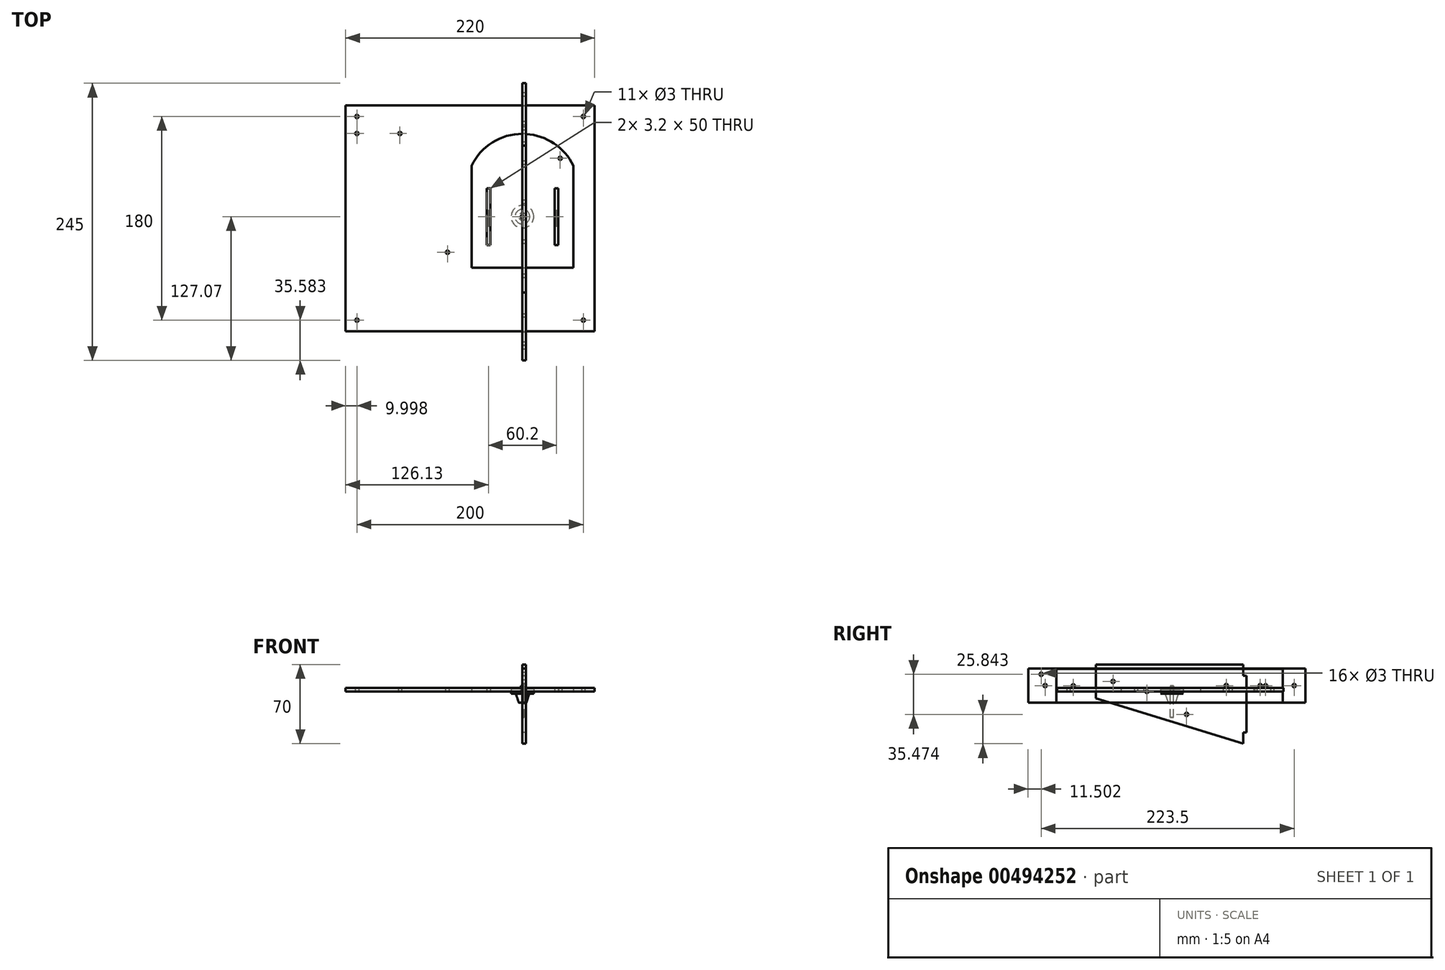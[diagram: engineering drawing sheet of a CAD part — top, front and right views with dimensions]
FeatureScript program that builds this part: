
annotation { "Feature Type Name" : "Feature", "Feature Type Description" : "" }
export const myFeature = defineFeature(function(context is Context, id is Id, definition is map)
    precondition{}
    {
        {
            var Q0;
            Q0=qCreatedBy(makeId("Right.planeOp"),FACE);
            var sketch = newSketch(context, id + "F0", { "sketchPlane" : qUnion([Q0])});
            skLineSegment(sketch, "E0", {"start": v(-67.11, 23.84) * mm, "end": v(62.89, 23.84) * mm});
            skLineSegment(sketch, "E1", {"start": v(-67.11, 23.84) * mm, "end": v(-67.11, -6.16) * mm});
            skLineSegment(sketch, "E2", {"start": v(62.89, 23.84) * mm, "end": v(62.89, -46.16) * mm});
            skLineSegment(sketch, "E3", {"start": v(-67.11, -6.16) * mm, "end": v(62.89, -46.16) * mm});
            skLineSegment(sketch, "E4.bottom", {"start": v(62.89, 13.84) * mm, "end": v(65.89, 13.84) * mm});
            skLineSegment(sketch, "E4.top", {"start": v(62.89, -36.16) * mm, "end": v(65.89, -36.16) * mm});
            skLineSegment(sketch, "E4.left", {"start": v(62.89, 13.84) * mm, "end": v(62.89, -36.16) * mm});
            skLineSegment(sketch, "E4.right", {"start": v(65.89, 13.84) * mm, "end": v(65.89, -36.16) * mm});
            skCircle(sketch, "E5", {"center": v(12.89, -20.32) * mm, "radius": 1.5 * mm});
            skSolve(sketch);
        }
        {
            var Q0;
            Q0=qCreatedBy(makeId("Right.planeOp"),FACE);
            var sketch = newSketch(context, id + "F1", { "sketchPlane" : qUnion([Q0])});
            skLineSegment(sketch, "E6.bottom", {"start": v(-127.07, 20.16) * mm, "end": v(117.93, 20.16) * mm});
            skLineSegment(sketch, "E6.top", {"start": v(-127.07, -9.84) * mm, "end": v(117.93, -9.84) * mm});
            skLineSegment(sketch, "E6.left", {"start": v(-127.07, 20.16) * mm, "end": v(-127.07, -9.84) * mm});
            skLineSegment(sketch, "E6.right", {"start": v(117.93, 20.16) * mm, "end": v(117.93, -9.84) * mm});
            skCircle(sketch, "E7", {"center": v(107.93, 5.16) * mm, "radius": 1.5 * mm});
            skCircle(sketch, "E8", {"center": v(77.93, 5.16) * mm, "radius": 1.5 * mm});
            skCircle(sketch, "E9", {"center": v(-115.57, 15.16) * mm, "radius": 1.5 * mm});
            skSolve(sketch);
        }
        {
            var Q0;
            Q0=qCreatedBy(makeId("Right.planeOp"),FACE);
            var sketch = newSketch(context, id + "F2", { "sketchPlane" : qUnion([Q0])});
            skLineSegment(sketch, "E10.bottom", {"start": v(-102.26, 20) * mm, "end": v(97.74, 20) * mm});
            skLineSegment(sketch, "E10.top", {"start": v(-102.26, -10) * mm, "end": v(97.74, -10) * mm});
            skLineSegment(sketch, "E10.left", {"start": v(-102.26, 20) * mm, "end": v(-102.26, -10) * mm});
            skLineSegment(sketch, "E10.right", {"start": v(97.74, 20) * mm, "end": v(97.74, -10) * mm});
            skCircle(sketch, "E11", {"center": v(-22.26, 0) * mm, "radius": 1.5 * mm});
            skSolve(sketch);
        }
        {
            var Q0;
            Q0 = qSketchRegion(id + "F0", true);
            extrude(context, id + "F3", {"entities" : qUnion([Q0]), "depth" : 3.2 * mm});
        }
        {
            var Q0;
            Q0=makeQuery(id+"F1.imprint","IMPRINT",FACE,{"disambiguationData":[TD([[makeQuery(id+"F1.imprint","IMPRINT",EDGE,{"derivedFrom":sQuery(id+"F1.wireOp",EDGE,"E6.bottom")}),-1.0]])]});
            extrude(context, id + "F4", {"entities" : qUnion([Q0]), "depth" : 3.2 * mm});
        }
        {
            var Q0;
            Q0=makeQuery(id+"F2.imprint","IMPRINT",FACE,{"disambiguationData":[TD([[makeQuery(id+"F2.imprint","IMPRINT",EDGE,{"derivedFrom":sQuery(id+"F2.wireOp",EDGE,"E10.bottom")}),-1.0]])]});
            extrude(context, id + "F5", {"entities" : qUnion([Q0]), "depth" : 3.2 * mm});
        }
        {
            var Q0;
            Q0=makeQuery(id+"F3.opExtrude","CAP_FACE",FACE,{"disambiguationData":[OSD([sQuery(id+"F0.wireOp",EDGE,"E0"),sQuery(id+"F0.wireOp",EDGE,"E1"),sQuery(id+"F0.wireOp",EDGE,"E2"),sQuery(id+"F0.wireOp",EDGE,"E3")])],"isStart":false});
            var sketch = newSketch(context, id + "F6", { "sketchPlane" : qUnion([Q0])});
            skCircle(sketch, "E12", {"center": v(-52.11, 8.84) * mm, "radius": 1.5 * mm});
            skSolve(sketch);
        }
        {
            var Q0;
            Q0=makeQuery(id+"F6.imprint","IMPRINT",FACE,{"disambiguationData":[TD([[makeQuery(id+"F6.imprint","IMPRINT",EDGE,{"derivedFrom":sQuery(id+"F6.wireOp",EDGE,"E12")}),1.0]])]});
            extrude(context, id + "F7", {"entities" : qUnion([Q0]), "operationType" : NewBodyOperationType.REMOVE, "endBound" : BoundingType.THROUGH_ALL, "oppositeDirection" : true, "depth" : 25 * mm});
        }
        {
            var Q0;
            Q0=makeQuery(id+"F4.opExtrude","CAP_FACE",FACE,{"disambiguationData":[OSD([sQuery(id+"F1.wireOp",EDGE,"E6.bottom"),sQuery(id+"F1.wireOp",EDGE,"E6.top"),sQuery(id+"F1.wireOp",EDGE,"E6.left"),sQuery(id+"F1.wireOp",EDGE,"E6.right")])],"isStart":false});
            var sketch = newSketch(context, id + "F8", { "sketchPlane" : qUnion([Q0])});
            skCircle(sketch, "E13", {"center": v(-112.07, 5.16) * mm, "radius": 1.5 * mm});
            skCircle(sketch, "E14", {"center": v(47.93, 5.16) * mm, "radius": 1.5 * mm});
            skSolve(sketch);
        }
        {
            var Q0;
            Q0=makeQuery(id+"F8.imprint","IMPRINT",FACE,{"disambiguationData":[TD([[makeQuery(id+"F8.imprint","IMPRINT",EDGE,{"derivedFrom":sQuery(id+"F8.wireOp",EDGE,"E13")}),1.0]])]});
            var Q1;
            Q1=makeQuery(id+"F8.imprint","IMPRINT",FACE,{"disambiguationData":[TD([[makeQuery(id+"F8.imprint","IMPRINT",EDGE,{"derivedFrom":sQuery(id+"F8.wireOp",EDGE,"E14")}),1.0]])]});
            extrude(context, id + "F9", {"entities" : qUnion([Q0, Q1]), "operationType" : NewBodyOperationType.REMOVE, "endBound" : BoundingType.THROUGH_ALL, "oppositeDirection" : true, "depth" : 25 * mm});
        }
        {
            var Q0;
            Q0=makeQuery(id+"F5.opExtrude","CAP_FACE",FACE,{"disambiguationData":[OSD([sQuery(id+"F2.wireOp",EDGE,"E10.bottom"),sQuery(id+"F2.wireOp",EDGE,"E10.top"),sQuery(id+"F2.wireOp",EDGE,"E10.left"),sQuery(id+"F2.wireOp",EDGE,"E10.right")])],"isStart":false});
            var sketch = newSketch(context, id + "F10", { "sketchPlane" : qUnion([Q0])});
            skCircle(sketch, "E15", {"center": v(-87.26, 5) * mm, "radius": 1.5 * mm});
            skCircle(sketch, "E16", {"center": v(82.74, 5) * mm, "radius": 1.5 * mm});
            skSolve(sketch);
        }
        {
            var Q0;
            Q0=makeQuery(id+"F10.imprint","IMPRINT",FACE,{"disambiguationData":[TD([[makeQuery(id+"F10.imprint","IMPRINT",EDGE,{"derivedFrom":sQuery(id+"F10.wireOp",EDGE,"E15")}),1.0]])]});
            var Q1;
            Q1=makeQuery(id+"F10.imprint","IMPRINT",FACE,{"disambiguationData":[TD([[makeQuery(id+"F10.imprint","IMPRINT",EDGE,{"derivedFrom":sQuery(id+"F10.wireOp",EDGE,"E16")}),1.0]])]});
            extrude(context, id + "F11", {"entities" : qUnion([Q0, Q1]), "operationType" : NewBodyOperationType.REMOVE, "endBound" : BoundingType.THROUGH_ALL, "oppositeDirection" : true, "depth" : 25 * mm});
        }
        {
            var Q0;
            Q0=qCreatedBy(makeId("Top.planeOp"),FACE);
            var sketch = newSketch(context, id + "F12", { "sketchPlane" : qUnion([Q0])});
            skLineSegment(sketch, "E17.bottom", {"start": v(-45, 45) * mm, "end": v(45, 45) * mm});
            skLineSegment(sketch, "E17.top", {"start": v(-45, -45) * mm, "end": v(45, -45) * mm});
            skLineSegment(sketch, "E17.left", {"start": v(-45, 45) * mm, "end": v(-45, -45) * mm});
            skLineSegment(sketch, "E17.right", {"start": v(45, 45) * mm, "end": v(45, -45) * mm});
            skLineSegment(sketch, "E18.bottom", {"start": v(-31.7, 25) * mm, "end": v(-28.5, 25) * mm});
            skLineSegment(sketch, "E18.top", {"start": v(-31.7, -25) * mm, "end": v(-28.5, -25) * mm});
            skLineSegment(sketch, "E18.left", {"start": v(-31.7, 25) * mm, "end": v(-31.7, -25) * mm});
            skLineSegment(sketch, "E18.right", {"start": v(-28.5, 25) * mm, "end": v(-28.5, -25) * mm});
            skLineSegment(sketch, "E19.bottom", {"start": v(28.5, 25) * mm, "end": v(31.7, 25) * mm});
            skLineSegment(sketch, "E19.top", {"start": v(28.5, -25) * mm, "end": v(31.7, -25) * mm});
            skLineSegment(sketch, "E19.left", {"start": v(28.5, 25) * mm, "end": v(28.5, -25) * mm});
            skLineSegment(sketch, "E19.right", {"start": v(31.7, 25) * mm, "end": v(31.7, -25) * mm});
            skArc(sketch, "E20", {"start": v(45, 45) * mm, "mid": v(0, 73.2) * mm, "end": v(-45, 45) * mm});
            skCircle(sketch, "E21", {"center": v(33.35, 51.62) * mm, "radius": 1.5 * mm});
            skSolve(sketch);
        }
        {
            var Q0;
            Q0=makeQuery(id+"F12.imprint","IMPRINT",FACE,{"disambiguationData":[TD([[makeQuery(id+"F12.imprint","IMPRINT",EDGE,{"derivedFrom":sQuery(id+"F12.wireOp",EDGE,"E17.bottom")}),-1.0]])]});
            var Q1;
            Q1=makeQuery(id+"F12.imprint","IMPRINT",FACE,{"disambiguationData":[TD([[makeQuery(id+"F12.imprint","IMPRINT",EDGE,{"derivedFrom":sQuery(id+"F12.wireOp",EDGE,"E17.bottom")}),1.0]])]});
            extrude(context, id + "F13", {"entities" : qUnion([Q0, Q1]), "depth" : 3.2 * mm, "offsetDistance" : 25 * mm});
        }
        {
            var Q0;
            Q0=qCreatedBy(makeId("Top.planeOp"),FACE);
            var sketch = newSketch(context, id + "F14", { "sketchPlane" : qUnion([Q0])});
            skLineSegment(sketch, "E22.bottom", {"start": v(-156.23, 98.51) * mm, "end": v(63.77, 98.51) * mm});
            skLineSegment(sketch, "E22.top", {"start": v(-156.23, -101.49) * mm, "end": v(63.77, -101.49) * mm});
            skLineSegment(sketch, "E22.left", {"start": v(-156.23, 98.51) * mm, "end": v(-156.23, -101.49) * mm});
            skLineSegment(sketch, "E22.right", {"start": v(63.77, 98.51) * mm, "end": v(63.77, -101.49) * mm});
            skCircle(sketch, "E23", {"center": v(-146.23, 88.51) * mm, "radius": 1.5 * mm});
            skCircle(sketch, "E24", {"center": v(-146.23, -91.49) * mm, "radius": 1.5 * mm});
            skCircle(sketch, "E25", {"center": v(53.77, 88.51) * mm, "radius": 1.5 * mm});
            skCircle(sketch, "E26", {"center": v(53.77, -91.49) * mm, "radius": 1.5 * mm});
            skCircle(sketch, "E27", {"center": v(-146.23, 73.51) * mm, "radius": 1.5 * mm});
            skCircle(sketch, "E28", {"center": v(-108.23, 73.51) * mm, "radius": 1.5 * mm});
            skSolve(sketch);
        }
        {
            var Q0;
            Q0 = qSketchRegion(id + "F14", true);
            extrude(context, id + "F15", {"entities" : qUnion([Q0]), "depth" : 3 * mm, "offsetDistance" : 25 * mm});
        }
        {
            var Q0;
            Q0=makeQuery(id+"F15.opExtrude","CAP_FACE",FACE,{"disambiguationData":[OSD([sQuery(id+"F14.wireOp",EDGE,"E22.bottom"),sQuery(id+"F14.wireOp",EDGE,"E22.top"),sQuery(id+"F14.wireOp",EDGE,"E22.left"),sQuery(id+"F14.wireOp",EDGE,"E22.right")])],"isStart":false});
            var sketch = newSketch(context, id + "F16", { "sketchPlane" : qUnion([Q0])});
            skCircle(sketch, "E29", {"center": v(-66.23, -31.49) * mm, "radius": 1.5 * mm});
            skSolve(sketch);
        }
        {
            var Q0;
            Q0=makeQuery(id+"F16.imprint","IMPRINT",FACE,{"disambiguationData":[TD([[makeQuery(id+"F16.imprint","IMPRINT",EDGE,{"derivedFrom":sQuery(id+"F16.wireOp",EDGE,"E29")}),1.0]])]});
            extrude(context, id + "F17", {"entities" : qUnion([Q0]), "operationType" : NewBodyOperationType.REMOVE, "oppositeDirection" : true, "depth" : 53 * mm, "offsetDistance" : 25 * mm});
        }
        {
            var Q0;
            Q0=makeQuery(id+"F13.opExtrude","CAP_FACE",FACE,{"disambiguationData":[OSD([sQuery(id+"F12.wireOp",EDGE,"E17.bottom"),sQuery(id+"F12.wireOp",EDGE,"E17.top"),sQuery(id+"F12.wireOp",EDGE,"E17.left"),sQuery(id+"F12.wireOp",EDGE,"E17.right")])],"isStart":false});
            var sketch = newSketch(context, id + "F18", { "sketchPlane" : qUnion([Q0])});
            skCircle(sketch, "E30", {"center": v(0, 0) * mm, "radius": 1.5 * mm});
            skSolve(sketch);
        }
        {
            var Q0;
            Q0=makeQuery(id+"F18.imprint","IMPRINT",FACE,{"disambiguationData":[TD([[makeQuery(id+"F18.imprint","IMPRINT",EDGE,{"derivedFrom":sQuery(id+"F18.wireOp",EDGE,"E30")}),1.0]])]});
            extrude(context, id + "F19", {"entities" : qUnion([Q0]), "operationType" : NewBodyOperationType.REMOVE, "oppositeDirection" : true, "depth" : 25 * mm, "offsetDistance" : 25 * mm});
        }
        {
            var Q0;
            Q0=qCreatedBy(makeId("Top.planeOp"),FACE);
            var sketch = newSketch(context, id + "F20", { "sketchPlane" : qUnion([Q0])});
            skCircle(sketch, "E31", {"center": v(0, 0) * mm, "radius": 10 * mm});
            skSolve(sketch);
        }
        {
            var Q0;
            Q0=makeQuery(id+"F20.imprint","IMPRINT",FACE,{"disambiguationData":[TD([[makeQuery(id+"F20.imprint","IMPRINT",EDGE,{"derivedFrom":sQuery(id+"F20.wireOp",EDGE,"E31")}),1.0]])]});
            extrude(context, id + "F21", {"entities" : qUnion([Q0]), "depth" : 4 * mm, "offsetDistance" : 25 * mm, "symmetric" : true});
        }
        {
            var Q0;
            Q0=makeQuery(id+"F21.opExtrude","CAP_FACE",FACE,{"disambiguationData":[OSD([sQuery(id+"F20.wireOp",EDGE,"E31")])],"isStart":false});
            var sketch = newSketch(context, id + "F22", { "sketchPlane" : qUnion([Q0])});
            skCircle(sketch, "E32", {"center": v(0, 0) * mm, "radius": 1.5 * mm});
            skSolve(sketch);
        }
        {
            var Q0;
            Q0=makeQuery(id+"F22.imprint","IMPRINT",FACE,{"disambiguationData":[TD([[makeQuery(id+"F22.imprint","IMPRINT",EDGE,{"derivedFrom":sQuery(id+"F22.wireOp",EDGE,"E32")}),1.0]])]});
            extrude(context, id + "F23", {"entities" : qUnion([Q0]), "operationType" : NewBodyOperationType.REMOVE, "oppositeDirection" : true, "depth" : 25 * mm, "offsetDistance" : 25 * mm});
        }
        {
            var Q0;
            Q0=qCreatedBy(makeId("Front.planeOp"),FACE);
            var sketch = newSketch(context, id + "F24", { "sketchPlane" : qUnion([Q0])});
            skLineSegment(sketch, "E33", {"start": v(0, -15.89) * mm, "end": v(0, 25.02) * mm, "construction": true});
            skLineSegment(sketch, "E34", {"start": v(-6.5, 0) * mm, "end": v(0, 0) * mm});
            skLineSegment(sketch, "E35", {"start": v(0, 0) * mm, "end": v(0, -10) * mm});
            skLineSegment(sketch, "E36", {"start": v(0, -10) * mm, "end": v(-3.23, -10) * mm});
            skLineSegment(sketch, "E37", {"start": v(-3.23, -10) * mm, "end": v(-6.5, 0) * mm});
            skLineSegment(sketch, "E38", {"start": v(-1.5, 0) * mm, "end": v(-1.5, 5) * mm});
            skLineSegment(sketch, "E39", {"start": v(-1.5, 5) * mm, "end": v(0, 5) * mm});
            skLineSegment(sketch, "E40", {"start": v(0, 5) * mm, "end": v(0, 0) * mm});
            skSolve(sketch);
        }
        {
            var Q0;
            Q0 = qSketchRegion(id + "F24", true);
            var Q1;
            Q1=sQuery(id+"F24.wireOp",EDGE,"E33");
            revolve(context, id + "F25", {"entities" : qUnion([Q0]), "axis" : qUnion([Q1]), "revolveType" : RevolveType.FULL});
        }
    });
